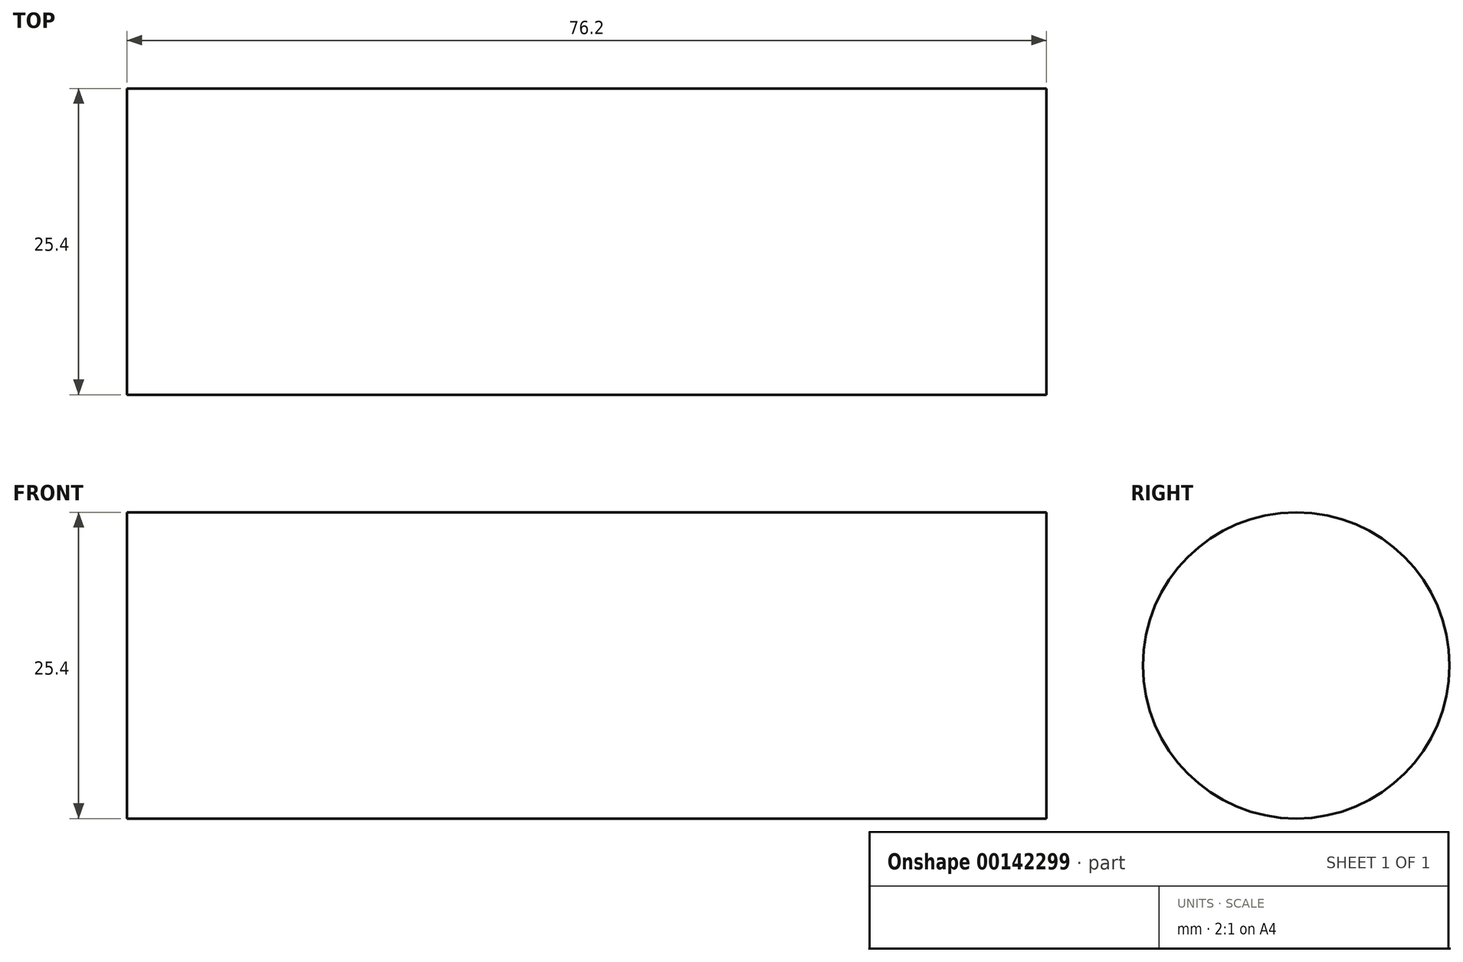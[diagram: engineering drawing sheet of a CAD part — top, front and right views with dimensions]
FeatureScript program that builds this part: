
annotation { "Feature Type Name" : "Feature", "Feature Type Description" : "" }
export const myFeature = defineFeature(function(context is Context, id is Id, definition is map)
    precondition{}
    {
        {
            var Q0;
            Q0=qCreatedBy(makeId("Right.planeOp"),FACE);
            var sketch = newSketch(context, id + "F0", { "sketchPlane" : qUnion([Q0])});
            skCircle(sketch, "E0", {"center": v(0, 0) * mm, "radius": 12.7 * mm});
            skSolve(sketch);
        }
        {
            var Q0;
            Q0 = qSketchRegion(id + "F0", true);
            extrude(context, id + "F1", {"entities" : qUnion([Q0]), "depth" : 76.2 * mm});
        }
    });
